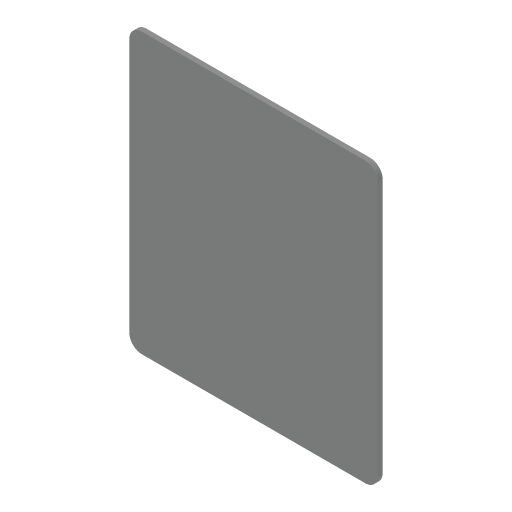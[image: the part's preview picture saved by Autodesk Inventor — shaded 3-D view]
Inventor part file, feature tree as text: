
AUTODESK INVENTOR PART (.ipt)
format: ipt  version: 2024.1 (Build 281209000, 209)  size: 91,648 bytes
history: native  units: mm
features: extrude x1, sketch x1
ambient origin geometry x8: Origin, YZ Plane, XZ Plane, XY Plane, X Axis, Y Axis, Z Axis, Center Point
bodies: Solid1 (feature_tree)
feature tree (2):
  extrude  "Extrusion1"  Depth=450.0mm
  sketch  "Sketch1"  dims[d0=400.0mm d1=450.0mm d2=20.0mm d3=8.0mm d4=0.0mm]
